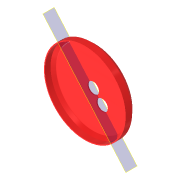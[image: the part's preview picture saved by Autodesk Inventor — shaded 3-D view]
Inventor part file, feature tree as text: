
AUTODESK INVENTOR PART (.ipt)
format: ipt  version: 2022 (Build 260153000, 153)  size: 182,784 bytes
history: native  units: mm
features: other x3, sketch x2, reference x2, revolve x1, fillet x1, extrude x1, plane x1
ambient origin geometry x8: Origin, YZ Plane, XZ Plane, XY Plane, X Axis, Y Axis, Z Axis, Center Point
bodies: Volumenkörper1 (feature_tree)
feature tree (11):
  revolve  "Umdrehung1"
  fillet  "Rundung1"  Radius=34.25mm
  extrude  "Extrusion1"  Depth=6.0mm
  plane  "Arbeitsebene1"
  sketch  "Skizze1"  dims[d1=1.0mm d2=6.0mm]
  sketch  "Skizze2"  dims[d3=10.0mm d4=1.0mm d5=1.0mm d6=90.0deg d7=1.0mm d8=12.0mm d9=12.0mm d10=10.0mm d11=0.0mm]
  reference  "Referenz1"
  reference  "Referenz2"
  other  "Anglerfish_bonne_mamman_m12large_flipped_v0.iam"
  other  "Anglerfish_Lightplate_Tislinkbridge:1"
  other  "Anglerfish_flipped_LidMoun:1"
